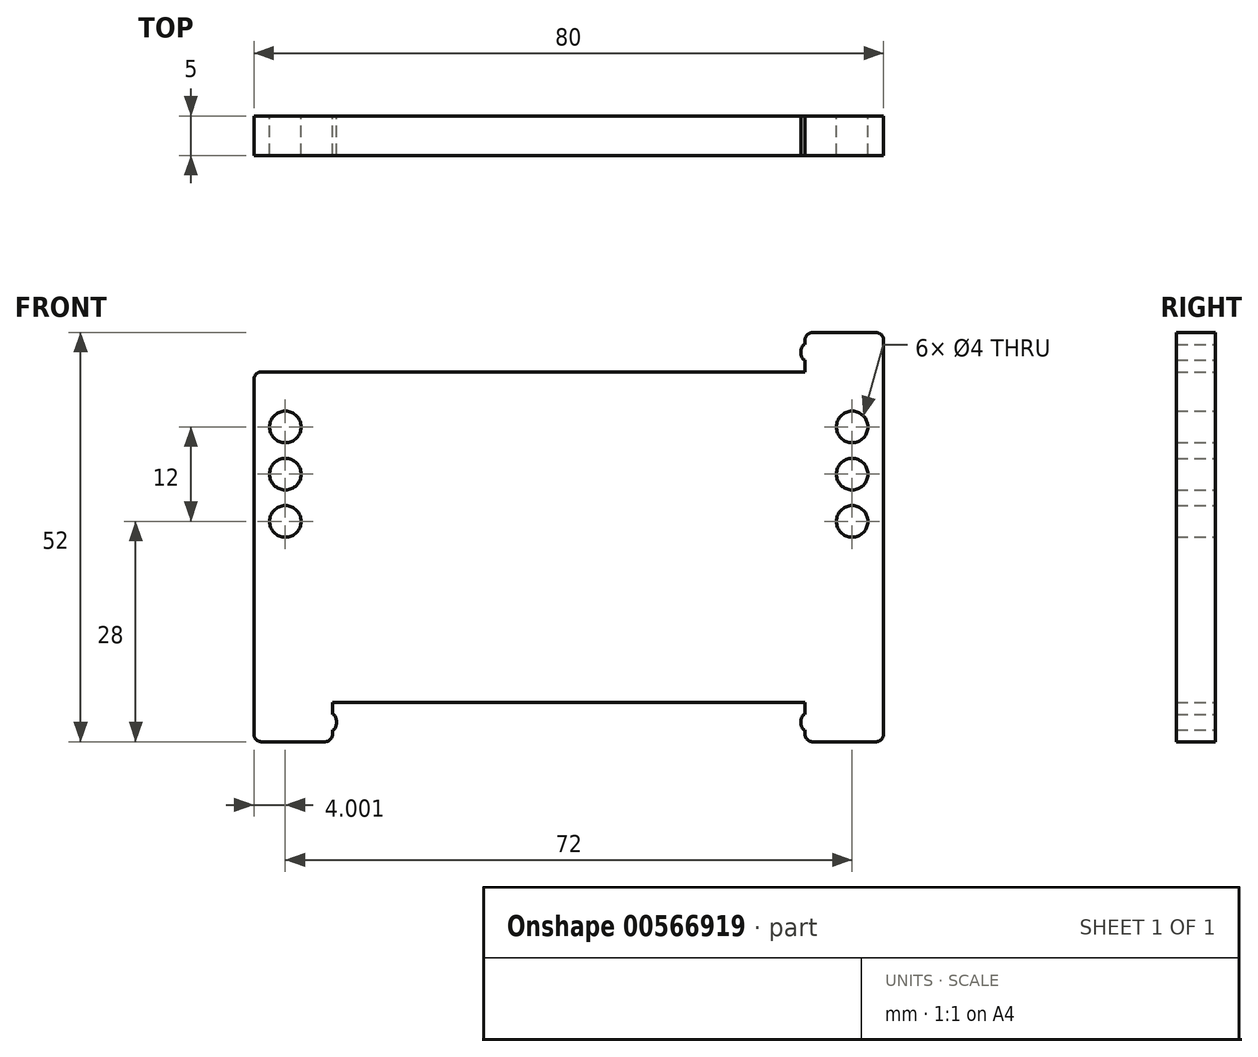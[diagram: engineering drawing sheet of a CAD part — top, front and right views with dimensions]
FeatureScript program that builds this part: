
annotation { "Feature Type Name" : "Feature", "Feature Type Description" : "" }
export const myFeature = defineFeature(function(context is Context, id is Id, definition is map)
    precondition{}
    {
        {
            assignVariable(context, id + "F0", {"name" : "th", "anyValue" : 5 * mm});
        }
        {
            var Q0;
            Q0=qCreatedBy(makeId("Front.planeOp"),FACE);
            var sketch = newSketch(context, id + "F1", { "sketchPlane" : qUnion([Q0])});
            skLineSegment(sketch, "E0.bottom", {"start": v(-47.13, 37.29) * mm, "end": v(32.87, 37.29) * mm});
            skLineSegment(sketch, "E0.top", {"start": v(-47.13, -4.71) * mm, "end": v(32.87, -4.71) * mm});
            skLineSegment(sketch, "E0.left", {"start": v(-47.13, 37.29) * mm, "end": v(-47.13, -4.71) * mm});
            skLineSegment(sketch, "E0.right", {"start": v(32.87, 37.29) * mm, "end": v(32.87, -4.71) * mm});
            skLineSegment(sketch, "E1.bottom", {"start": v(-47.13, 37.29) * mm, "end": v(-37.13, 37.29) * mm});
            skLineSegment(sketch, "E1.top", {"start": v(-47.13, 42.29) * mm, "end": v(-37.13, 42.29) * mm});
            skLineSegment(sketch, "E1.left", {"start": v(-47.13, 37.29) * mm, "end": v(-47.13, 42.29) * mm});
            skLineSegment(sketch, "E1.right", {"start": v(-37.13, 37.29) * mm, "end": v(-37.13, 38.79) * mm});
            skLineSegment(sketch, "E2", {"start": v(-7.13, 37.29) * mm, "end": v(-7.13, -4.71) * mm, "construction": true});
            skLineSegment(sketch, "E3", {"start": v(-47.13, 16.29) * mm, "end": v(32.87, 16.29) * mm, "construction": true});
            skLineSegment(sketch, "E4.MirrorCS", {"start": v(22.87, 37.29) * mm, "end": v(22.87, 38.79) * mm});
            skLineSegment(sketch, "E5.MirrorCS", {"start": v(32.87, 42.29) * mm, "end": v(22.87, 42.29) * mm});
            skLineSegment(sketch, "E6.MirrorCS", {"start": v(32.87, 37.29) * mm, "end": v(32.87, 42.29) * mm});
            skEllipticalArc(sketch, "E7", {});
            skEllipticalArc(sketch, "E8.MirrorC", {});
            skEllipticalArc(sketch, "E9.MirrorC", {});
            skEllipticalArc(sketch, "E10.MirrorC", {});
            skLineSegment(sketch, "E11.MirrorCS", {"start": v(22.87, -4.71) * mm, "end": v(22.87, -6.21) * mm});
            skLineSegment(sketch, "E12.MirrorCS", {"start": v(32.87, -9.71) * mm, "end": v(22.87, -9.71) * mm});
            skLineSegment(sketch, "E13.MirrorCS", {"start": v(-47.13, -9.71) * mm, "end": v(-37.13, -9.71) * mm});
            skLineSegment(sketch, "E14.MirrorCS", {"start": v(-47.13, -4.71) * mm, "end": v(-47.13, -9.71) * mm});
            skLineSegment(sketch, "E15.MirrorCS", {"start": v(-37.13, -4.71) * mm, "end": v(-37.13, -6.21) * mm});
            skLineSegment(sketch, "E16.MirrorCS", {"start": v(32.87, -4.71) * mm, "end": v(32.87, -9.71) * mm});
            skCircle(sketch, "E17", {"center": v(-43.13, 18.29) * mm, "radius": 2 * mm});
            skCircle(sketch, "E18", {"center": v(-43.13, 24.29) * mm, "radius": 2 * mm});
            skCircle(sketch, "E19", {"center": v(-43.13, 30.29) * mm, "radius": 2 * mm});
            skLineSegment(sketch, "E20", {"start": v(-43.13, 18.29) * mm, "end": v(-43.13, 32.29) * mm, "construction": true});
            skCircle(sketch, "E21.MirrorC", {"center": v(28.87, 24.29) * mm, "radius": 2 * mm});
            skCircle(sketch, "E22.MirrorC", {"center": v(28.87, 30.29) * mm, "radius": 2 * mm});
            skCircle(sketch, "E23.MirrorC", {"center": v(28.87, 18.29) * mm, "radius": 2 * mm});
            skLineSegment(sketch, "E24.trimOffspring", {"start": v(22.87, 39.79) * mm, "end": v(22.87, 42.29) * mm});
            skLineSegment(sketch, "E25.trimOffspring", {"start": v(-37.13, 39.79) * mm, "end": v(-37.13, 42.29) * mm});
            skLineSegment(sketch, "E26.trimOffspring", {"start": v(-37.13, -7.21) * mm, "end": v(-37.13, -9.71) * mm});
            skLineSegment(sketch, "E27.trimOffspring", {"start": v(22.87, -7.21) * mm, "end": v(22.87, -9.71) * mm});
            const initialGuessF1  = {"E7": [-0.03712881304323674, 0.03978960806931597, 0, 1, 0.001, 0.0005, 3.141592653589793, 0], "E8.MirrorC": [0.02287118695676327, 0.039789608069315974, 0, 1, 0.001, 0.0005, 0, 3.141592653589793], "E9.MirrorC": [-0.03712881304323674, -0.007210391930684045, 0, -1, 0.001, 0.0005, 0, 3.141592653589793], "E10.MirrorC": [0.022871186956763274, -0.007210391930684051, 0, -1, 0.001, 0.0005, 3.141592653589793, 0]};
            skSetInitialGuess(sketch, initialGuessF1);
            skSolve(sketch);
        }
        {
            var Q0;
            {var subQ2=sQuery(id+"F1.wireOp",EDGE,"E0.left");Q0=makeQuery(id+"F1.imprint","IMPRINT",FACE,{"disambiguationData":[TD([[makeQuery(id+"F1.imprint","IMPRINT",EDGE,{"derivedFrom":subQ2}),1.0]])]});}
            var Q1;
            Q1=makeQuery(id+"F1.imprint","IMPRINT",FACE,{"disambiguationData":[TD([[makeQuery(id+"F1.imprint","IMPRINT",EDGE,{"derivedFrom":sQuery(id+"F1.wireOp",EDGE,"E1.bottom")}),1.0]])]});
            var Q2;
            {var subQ3=sQuery(id+"F1.wireOp",EDGE,"E4.MirrorCS");Q2=makeQuery(id+"F1.imprint","IMPRINT",FACE,{"disambiguationData":[TD([[makeQuery(id+"F1.imprint","IMPRINT",EDGE,{"derivedFrom":subQ3}),-1.0]])]});}
            var Q3;
            {var subQ1=sQuery(id+"F1.wireOp",EDGE,"E10.MirrorC");Q3=makeQuery(id+"F1.imprint","IMPRINT",FACE,{"disambiguationData":[TD([[makeQuery(id+"F1.imprint","IMPRINT",EDGE,{"derivedFrom":subQ1}),1.0]])]});}
            var Q4;
            {var subQ3=sQuery(id+"F1.wireOp",EDGE,"E9.MirrorC");Q4=makeQuery(id+"F1.imprint","IMPRINT",FACE,{"disambiguationData":[TD([[makeQuery(id+"F1.imprint","IMPRINT",EDGE,{"derivedFrom":subQ3}),1.0]])]});}
            extrude(context, id + "F2", {"entities" : qUnion([Q0, Q1, Q2, Q3, Q4]), "depth" : getVariable(context, 'th'), "offsetDistance" : 25 * mm});
        }
        {
            var Q0;
            Q0=makeQuery(id+"F2.opExtrude","SWEPT_EDGE",EDGE,{"disambiguationData":[OSD([sQuery(id+"F1.wireOp",EDGE,"E1.top"),sQuery(id+"F1.wireOp",EDGE,"E1.left")])]});
            var Q1;
            Q1=makeQuery(id+"F2.opExtrude","SWEPT_EDGE",EDGE,{"disambiguationData":[OSD([sQuery(id+"F1.wireOp",EDGE,"E1.top"),sQuery(id+"F1.wireOp",EDGE,"E25.trimOffspring")])]});
            var Q2;
            Q2=makeQuery(id+"F2.opExtrude","SWEPT_EDGE",EDGE,{"disambiguationData":[OSD([sQuery(id+"F1.wireOp",EDGE,"E5.MirrorCS"),sQuery(id+"F1.wireOp",EDGE,"E24.trimOffspring")])]});
            var Q3;
            Q3=makeQuery(id+"F2.opExtrude","SWEPT_EDGE",EDGE,{"disambiguationData":[OSD([sQuery(id+"F1.wireOp",EDGE,"E5.MirrorCS"),sQuery(id+"F1.wireOp",EDGE,"E6.MirrorCS")])]});
            var Q4;
            Q4=makeQuery(id+"F2.opExtrude","SWEPT_EDGE",EDGE,{"disambiguationData":[OSD([sQuery(id+"F1.wireOp",EDGE,"E12.MirrorCS"),sQuery(id+"F1.wireOp",EDGE,"E27.trimOffspring")])]});
            var Q5;
            Q5=makeQuery(id+"F2.opExtrude","SWEPT_EDGE",EDGE,{"disambiguationData":[OSD([sQuery(id+"F1.wireOp",EDGE,"E12.MirrorCS"),sQuery(id+"F1.wireOp",EDGE,"E16.MirrorCS")])]});
            var Q6;
            Q6=makeQuery(id+"F2.opExtrude","SWEPT_EDGE",EDGE,{"disambiguationData":[OSD([sQuery(id+"F1.wireOp",EDGE,"E13.MirrorCS"),sQuery(id+"F1.wireOp",EDGE,"E14.MirrorCS")])]});
            var Q7;
            Q7=makeQuery(id+"F2.opExtrude","SWEPT_EDGE",EDGE,{"disambiguationData":[OSD([sQuery(id+"F1.wireOp",EDGE,"E13.MirrorCS"),sQuery(id+"F1.wireOp",EDGE,"E26.trimOffspring")])]});
            fillet(context, id + "F3", {"entities" : qUnion([Q0, Q1, Q2, Q3, Q4, Q5, Q6, Q7]), "radius" : 1 * mm, "tangentPropagation" : true, "allowEdgeOverflow" : false});
        }
    });
